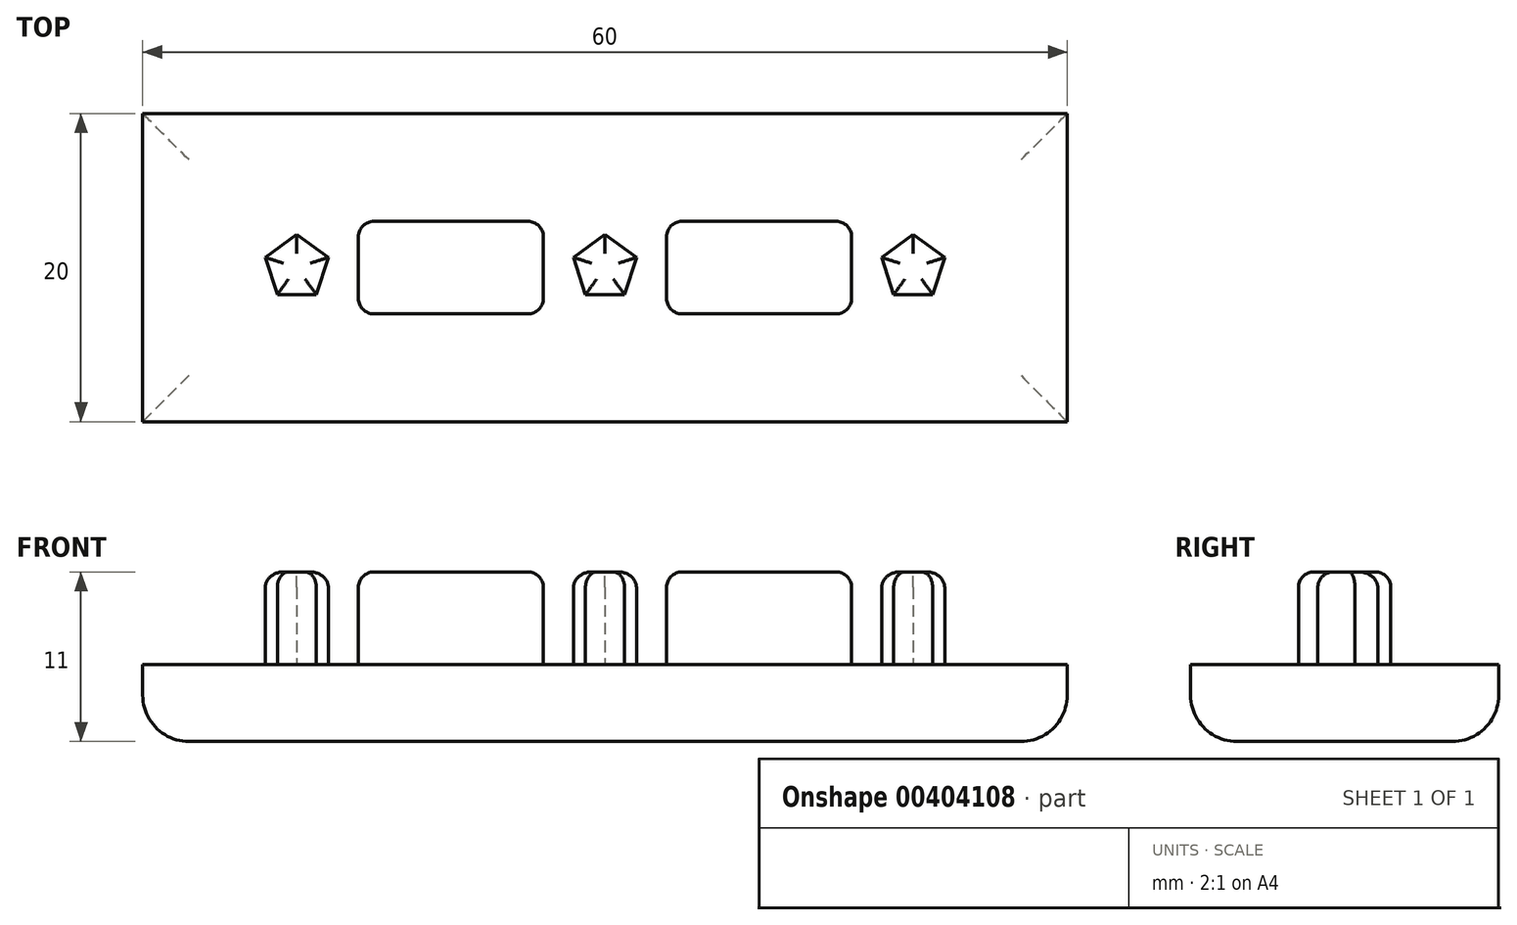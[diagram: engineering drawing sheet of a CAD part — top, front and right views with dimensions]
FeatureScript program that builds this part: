
annotation { "Feature Type Name" : "Feature", "Feature Type Description" : "" }
export const myFeature = defineFeature(function(context is Context, id is Id, definition is map)
    precondition{}
    {
        {
            var Q0;
            Q0=qCreatedBy(makeId("Top.planeOp"),FACE);
            var sketch = newSketch(context, id + "F0", { "sketchPlane" : qUnion([Q0])});
            skLineSegment(sketch, "E0.bottom", {"start": v(0, 20) * mm, "end": v(60, 20) * mm});
            skLineSegment(sketch, "E0.top", {"start": v(0, 0) * mm, "end": v(60, 0) * mm});
            skLineSegment(sketch, "E0.left", {"start": v(0, 20) * mm, "end": v(0, 0) * mm});
            skLineSegment(sketch, "E0.right", {"start": v(60, 20) * mm, "end": v(60, 0) * mm});
            skSolve(sketch);
        }
        {
            var Q0;
            Q0=makeQuery(id+"F0.imprint","IMPRINT",FACE,{"disambiguationData":[TD([[makeQuery(id+"F0.imprint","IMPRINT",EDGE,{"derivedFrom":sQuery(id+"F0.wireOp",EDGE,"E0.bottom")}),-1.0]])]});
            var sketch = newSketch(context, id + "F1", { "sketchPlane" : qUnion([Q0])});
            skCircle(sketch, "E1.cCircle", {"center": v(10, 10) * mm, "radius": 1.74 * mm, "construction": true});
            skLineSegment(sketch, "E1.0", {"start": v(11.26, 8.26) * mm, "end": v(8.74, 8.26) * mm});
            skLineSegment(sketch, "E1.1", {"start": v(8.74, 8.26) * mm, "end": v(7.96, 10.66) * mm});
            skLineSegment(sketch, "E1.2", {"start": v(7.96, 10.66) * mm, "end": v(10, 12.15) * mm});
            skLineSegment(sketch, "E1.3", {"start": v(10, 12.15) * mm, "end": v(12.04, 10.66) * mm});
            skLineSegment(sketch, "E1.4", {"start": v(12.04, 10.66) * mm, "end": v(11.26, 8.26) * mm});
            skPoint(sketch, "E1.0.midPoint", {"position": v(10, 8.26) * mm});
            skCircle(sketch, "E2.cCircle", {"center": v(30, 10) * mm, "radius": 1.74 * mm, "construction": true});
            skLineSegment(sketch, "E2.0", {"start": v(27.96, 10.66) * mm, "end": v(30, 12.15) * mm});
            skLineSegment(sketch, "E2.1", {"start": v(30, 12.15) * mm, "end": v(32.04, 10.66) * mm});
            skLineSegment(sketch, "E2.2", {"start": v(32.04, 10.66) * mm, "end": v(31.26, 8.26) * mm});
            skLineSegment(sketch, "E2.3", {"start": v(31.26, 8.26) * mm, "end": v(28.74, 8.26) * mm});
            skLineSegment(sketch, "E2.4", {"start": v(28.74, 8.26) * mm, "end": v(27.96, 10.66) * mm});
            skPoint(sketch, "E2.0.midPoint", {"position": v(28.98, 11.4) * mm});
            skCircle(sketch, "E3.cCircle", {"center": v(50, 10) * mm, "radius": 1.74 * mm, "construction": true});
            skLineSegment(sketch, "E3.0", {"start": v(47.96, 10.66) * mm, "end": v(50, 12.15) * mm});
            skLineSegment(sketch, "E3.1", {"start": v(50, 12.15) * mm, "end": v(52.04, 10.66) * mm});
            skLineSegment(sketch, "E3.2", {"start": v(52.04, 10.66) * mm, "end": v(51.26, 8.26) * mm});
            skLineSegment(sketch, "E3.3", {"start": v(51.26, 8.26) * mm, "end": v(48.74, 8.26) * mm});
            skLineSegment(sketch, "E3.4", {"start": v(48.74, 8.26) * mm, "end": v(47.96, 10.66) * mm});
            skPoint(sketch, "E3.0.midPoint", {"position": v(48.98, 11.4) * mm});
            skLineSegment(sketch, "E4.bottom", {"start": v(14, 13) * mm, "end": v(26, 13) * mm});
            skLineSegment(sketch, "E4.top", {"start": v(14, 7) * mm, "end": v(26, 7) * mm});
            skLineSegment(sketch, "E4.left", {"start": v(14, 13) * mm, "end": v(14, 7) * mm});
            skLineSegment(sketch, "E4.right", {"start": v(26, 13) * mm, "end": v(26, 7) * mm});
            skLineSegment(sketch, "E5.bottom", {"start": v(34, 13) * mm, "end": v(46, 13) * mm});
            skLineSegment(sketch, "E5.top", {"start": v(34, 7) * mm, "end": v(46, 7) * mm});
            skLineSegment(sketch, "E5.left", {"start": v(34, 13) * mm, "end": v(34, 7) * mm});
            skLineSegment(sketch, "E5.right", {"start": v(46, 13) * mm, "end": v(46, 7) * mm});
            skPoint(sketch, "E6", {"position": v(14, 10) * mm});
            skPoint(sketch, "E7", {"position": v(20, 13) * mm});
            skSolve(sketch);
        }
        {
            var Q0;
            Q0=makeQuery(id+"F0.imprint","IMPRINT",FACE,{"disambiguationData":[TD([[makeQuery(id+"F0.imprint","IMPRINT",EDGE,{"derivedFrom":sQuery(id+"F0.wireOp",EDGE,"E0.bottom")}),-1.0]])]});
            extrude(context, id + "F2", {"entities" : qUnion([Q0]), "oppositeDirection" : true, "depth" : 5 * mm});
        }
        {
            var Q0;
            Q0=qSketchRegion(id+"F1",true);
            extrude(context, id + "F3", {"entities" : qUnion([Q0]), "operationType" : NewBodyOperationType.ADD, "depth" : 6 * mm});
        }
        {
            var Q0;
            Q0=makeQuery(id+"F2.opExtrude","CAP_EDGE",EDGE,{"disambiguationData":[OSD([sQuery(id+"F0.wireOp",EDGE,"E0.left")])],"isStart":false});
            var Q1;
            Q1=makeQuery(id+"F2.opExtrude","CAP_EDGE",EDGE,{"disambiguationData":[OSD([sQuery(id+"F0.wireOp",EDGE,"E0.top")])],"isStart":false});
            var Q2;
            Q2=makeQuery(id+"F2.opExtrude","CAP_EDGE",EDGE,{"disambiguationData":[OSD([sQuery(id+"F0.wireOp",EDGE,"E0.right")])],"isStart":false});
            var Q3;
            Q3=makeQuery(id+"F2.opExtrude","CAP_EDGE",EDGE,{"disambiguationData":[OSD([sQuery(id+"F0.wireOp",EDGE,"E0.bottom")])],"isStart":false});
            fillet(context, id + "F4", {"entities" : qUnion([Q0, Q1, Q2, Q3]), "radius" : 3 * mm, "tangentPropagation" : true, "allowEdgeOverflow" : false});
        }
        {
            var Q0;
            Q0=makeQuery(id+"F3.opExtrude","CAP_EDGE",EDGE,{"disambiguationData":[OSD([sQuery(id+"F1.wireOp",EDGE,"E1.2")])],"isStart":false});
            var Q1;
            Q1=makeQuery(id+"F3.opExtrude","CAP_EDGE",EDGE,{"disambiguationData":[OSD([sQuery(id+"F1.wireOp",EDGE,"E1.1")])],"isStart":false});
            var Q2;
            Q2=makeQuery(id+"F3.opExtrude","CAP_EDGE",EDGE,{"disambiguationData":[OSD([sQuery(id+"F1.wireOp",EDGE,"E1.0")])],"isStart":false});
            var Q3;
            Q3=makeQuery(id+"F3.opExtrude","CAP_EDGE",EDGE,{"disambiguationData":[OSD([sQuery(id+"F1.wireOp",EDGE,"E1.4")])],"isStart":false});
            var Q4;
            Q4=makeQuery(id+"F3.opExtrude","CAP_EDGE",EDGE,{"disambiguationData":[OSD([sQuery(id+"F1.wireOp",EDGE,"E1.3")])],"isStart":false});
            var Q5;
            Q5=makeQuery(id+"F3.opExtrude","CAP_EDGE",EDGE,{"disambiguationData":[OSD([sQuery(id+"F1.wireOp",EDGE,"E2.0")])],"isStart":false});
            var Q6;
            Q6=makeQuery(id+"F3.opExtrude","CAP_EDGE",EDGE,{"disambiguationData":[OSD([sQuery(id+"F1.wireOp",EDGE,"E2.4")])],"isStart":false});
            var Q7;
            Q7=makeQuery(id+"F3.opExtrude","CAP_EDGE",EDGE,{"disambiguationData":[OSD([sQuery(id+"F1.wireOp",EDGE,"E2.3")])],"isStart":false});
            var Q8;
            Q8=makeQuery(id+"F3.opExtrude","CAP_EDGE",EDGE,{"disambiguationData":[OSD([sQuery(id+"F1.wireOp",EDGE,"E2.2")])],"isStart":false});
            var Q9;
            Q9=makeQuery(id+"F3.opExtrude","CAP_EDGE",EDGE,{"disambiguationData":[OSD([sQuery(id+"F1.wireOp",EDGE,"E2.1")])],"isStart":false});
            var Q10;
            Q10=makeQuery(id+"F3.opExtrude","CAP_EDGE",EDGE,{"disambiguationData":[OSD([sQuery(id+"F1.wireOp",EDGE,"E3.2")])],"isStart":false});
            var Q11;
            Q11=makeQuery(id+"F3.opExtrude","CAP_EDGE",EDGE,{"disambiguationData":[OSD([sQuery(id+"F1.wireOp",EDGE,"E3.3")])],"isStart":false});
            var Q12;
            Q12=makeQuery(id+"F3.opExtrude","CAP_EDGE",EDGE,{"disambiguationData":[OSD([sQuery(id+"F1.wireOp",EDGE,"E3.4")])],"isStart":false});
            var Q13;
            Q13=makeQuery(id+"F3.opExtrude","CAP_EDGE",EDGE,{"disambiguationData":[OSD([sQuery(id+"F1.wireOp",EDGE,"E3.0")])],"isStart":false});
            var Q14;
            Q14=makeQuery(id+"F3.opExtrude","CAP_EDGE",EDGE,{"disambiguationData":[OSD([sQuery(id+"F1.wireOp",EDGE,"E3.1")])],"isStart":false});
            var Q15;
            Q15=makeQuery(id+"F3.opExtrude","SWEPT_EDGE",EDGE,{"disambiguationData":[OSD([sQuery(id+"F1.wireOp",EDGE,"E4.top"),sQuery(id+"F1.wireOp",EDGE,"E4.left")])]});
            var Q16;
            Q16=makeQuery(id+"F3.opExtrude","SWEPT_EDGE",EDGE,{"disambiguationData":[OSD([sQuery(id+"F1.wireOp",EDGE,"E4.top"),sQuery(id+"F1.wireOp",EDGE,"E4.right")])]});
            var Q17;
            Q17=makeQuery(id+"F3.opExtrude","SWEPT_EDGE",EDGE,{"disambiguationData":[OSD([sQuery(id+"F1.wireOp",EDGE,"E4.bottom"),sQuery(id+"F1.wireOp",EDGE,"E4.right")])]});
            var Q18;
            Q18=makeQuery(id+"F3.opExtrude","SWEPT_EDGE",EDGE,{"disambiguationData":[OSD([sQuery(id+"F1.wireOp",EDGE,"E4.bottom"),sQuery(id+"F1.wireOp",EDGE,"E4.left")])]});
            var Q19;
            Q19=makeQuery(id+"F3.opExtrude","SWEPT_EDGE",EDGE,{"disambiguationData":[OSD([sQuery(id+"F1.wireOp",EDGE,"E5.bottom"),sQuery(id+"F1.wireOp",EDGE,"E5.left")])]});
            var Q20;
            Q20=makeQuery(id+"F3.opExtrude","SWEPT_EDGE",EDGE,{"disambiguationData":[OSD([sQuery(id+"F1.wireOp",EDGE,"E5.top"),sQuery(id+"F1.wireOp",EDGE,"E5.left")])]});
            var Q21;
            Q21=makeQuery(id+"F3.opExtrude","SWEPT_EDGE",EDGE,{"disambiguationData":[OSD([sQuery(id+"F1.wireOp",EDGE,"E5.bottom"),sQuery(id+"F1.wireOp",EDGE,"E5.right")])]});
            var Q22;
            Q22=makeQuery(id+"F3.opExtrude","SWEPT_EDGE",EDGE,{"disambiguationData":[OSD([sQuery(id+"F1.wireOp",EDGE,"E5.top"),sQuery(id+"F1.wireOp",EDGE,"E5.right")])]});
            var Q23;
            Q23=makeQuery(id+"F3.opExtrude","CAP_EDGE",EDGE,{"disambiguationData":[OSD([sQuery(id+"F1.wireOp",EDGE,"E4.left")])],"isStart":false});
            var Q24;
            Q24=makeQuery(id+"F3.opExtrude","CAP_EDGE",EDGE,{"disambiguationData":[OSD([sQuery(id+"F1.wireOp",EDGE,"E4.bottom")])],"isStart":false});
            var Q25;
            Q25=makeQuery(id+"F3.opExtrude","CAP_EDGE",EDGE,{"disambiguationData":[OSD([sQuery(id+"F1.wireOp",EDGE,"E4.right")])],"isStart":false});
            var Q26;
            Q26=makeQuery(id+"F3.opExtrude","CAP_EDGE",EDGE,{"disambiguationData":[OSD([sQuery(id+"F1.wireOp",EDGE,"E4.top")])],"isStart":false});
            var Q27;
            Q27=makeQuery(id+"F3.opExtrude","CAP_EDGE",EDGE,{"disambiguationData":[OSD([sQuery(id+"F1.wireOp",EDGE,"E5.left")])],"isStart":false});
            var Q28;
            Q28=makeQuery(id+"F3.opExtrude","CAP_EDGE",EDGE,{"disambiguationData":[OSD([sQuery(id+"F1.wireOp",EDGE,"E5.bottom")])],"isStart":false});
            var Q29;
            Q29=makeQuery(id+"F3.opExtrude","CAP_EDGE",EDGE,{"disambiguationData":[OSD([sQuery(id+"F1.wireOp",EDGE,"E5.right")])],"isStart":false});
            var Q30;
            Q30=makeQuery(id+"F3.opExtrude","CAP_EDGE",EDGE,{"disambiguationData":[OSD([sQuery(id+"F1.wireOp",EDGE,"E5.top")])],"isStart":false});
            fillet(context, id + "F5", {"entities" : qUnion([Q0, Q1, Q2, Q3, Q4, Q5, Q6, Q7, Q8, Q9, Q10, Q11, Q12, Q13, Q14, Q15, Q16, Q17, Q18, Q19, Q20, Q21, Q22, Q23, Q24, Q25, Q26, Q27, Q28, Q29, Q30]), "radius" : 1 * mm, "tangentPropagation" : true, "allowEdgeOverflow" : false});
        }
    });
